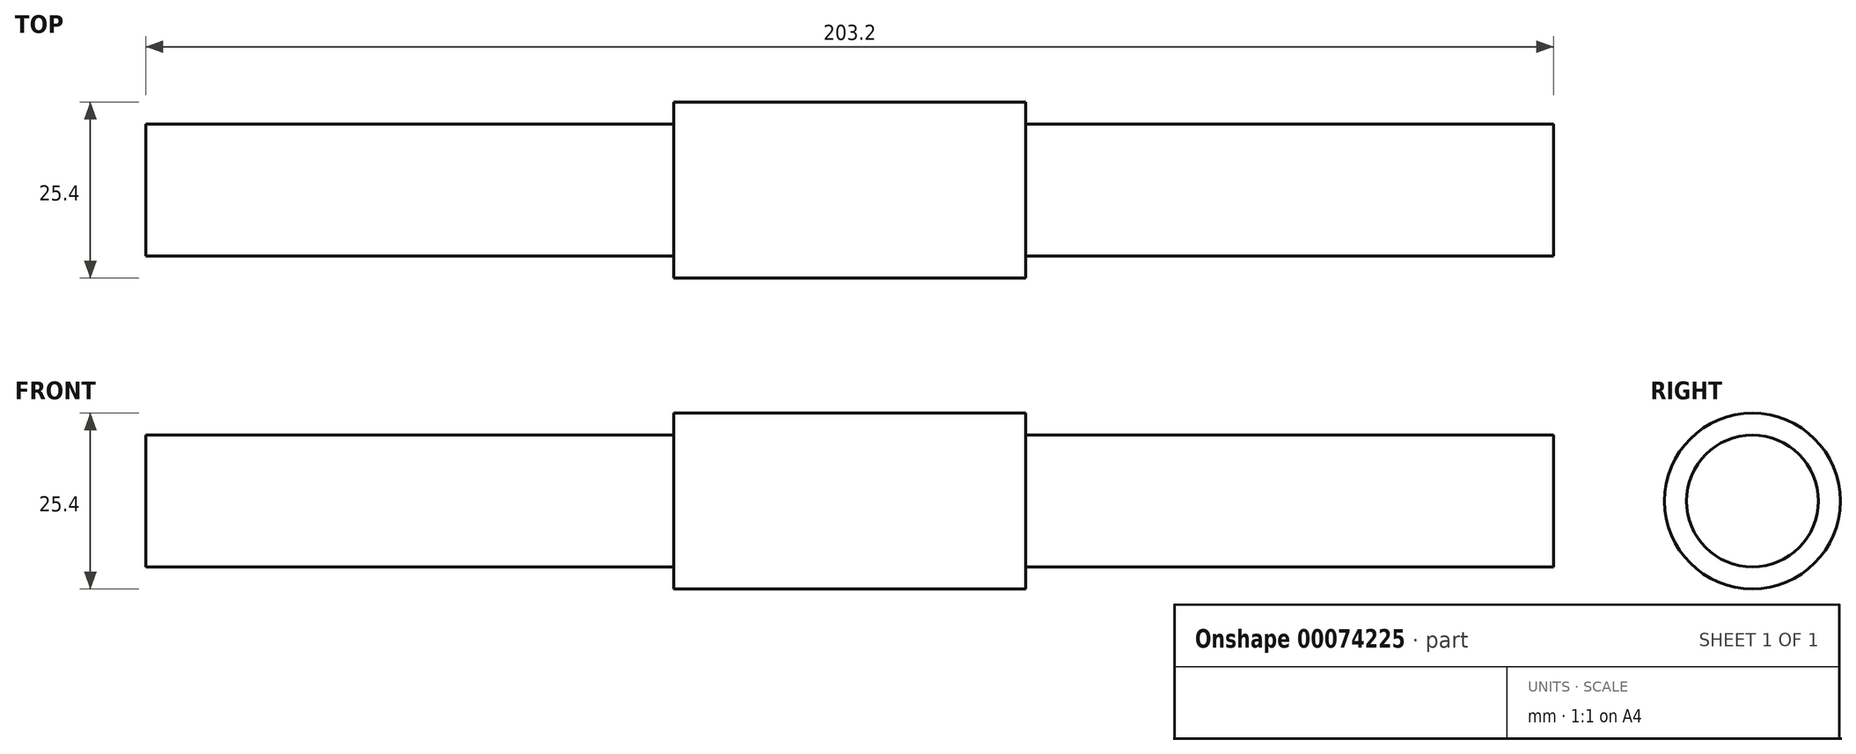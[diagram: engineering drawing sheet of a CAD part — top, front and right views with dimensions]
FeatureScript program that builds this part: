
annotation { "Feature Type Name" : "Feature", "Feature Type Description" : "" }
export const myFeature = defineFeature(function(context is Context, id is Id, definition is map)
    precondition{}
    {
        {
            var Q0;
            Q0=qCreatedBy(makeId("Right.planeOp"),FACE);
            var sketch = newSketch(context, id + "F0", { "sketchPlane" : qUnion([Q0])});
            skCircle(sketch, "E0", {"center": v(0, 0) * mm, "radius": 12.7 * mm});
            skSolve(sketch);
        }
        {
            var Q0;
            Q0=makeQuery(id+"F0.imprint","IMPRINT",FACE,{"disambiguationData":[TD([[makeQuery(id+"F0.imprint","IMPRINT",EDGE,{"derivedFrom":sQuery(id+"F0.wireOp",EDGE,"E0")}),1.0]])]});
            extrude(context, id + "F1", {"entities" : qUnion([Q0]), "endBound" : BoundingType.SYMMETRIC, "depth" : 50.8 * mm});
        }
        {
            var Q0;
            Q0=makeQuery(id+"F1.opExtrude","CAP_FACE",FACE,{"disambiguationData":[OSD([sQuery(id+"F0.wireOp",EDGE,"E0")])],"isStart":false});
            var sketch = newSketch(context, id + "F2", { "sketchPlane" : qUnion([Q0])});
            skCircle(sketch, "E1", {"center": v(0, 0) * mm, "radius": 9.53 * mm});
            skSolve(sketch);
        }
        {
            var Q0;
            Q0=qSketchRegion(id+"F2",true);
            extrude(context, id + "F3", {"entities" : qUnion([Q0]), "operationType" : NewBodyOperationType.ADD, "endBound" : BoundingType.SYMMETRIC, "depth" : 152.4 * mm});
        }
        {
            var Q0;
            Q0=makeQuery(id+"F1.opExtrude","CAP_FACE",FACE,{"disambiguationData":[OSD([sQuery(id+"F0.wireOp",EDGE,"E0")])],"isStart":true});
            var sketch = newSketch(context, id + "F4", { "sketchPlane" : qUnion([Q0])});
            skCircle(sketch, "E2", {"center": v(0, 0) * mm, "radius": 9.53 * mm});
            skSolve(sketch);
        }
        {
            var Q0;
            Q0=qSketchRegion(id+"F4",true);
            extrude(context, id + "F5", {"entities" : qUnion([Q0]), "operationType" : NewBodyOperationType.ADD, "endBound" : BoundingType.SYMMETRIC, "depth" : 152.4 * mm});
        }
    });
